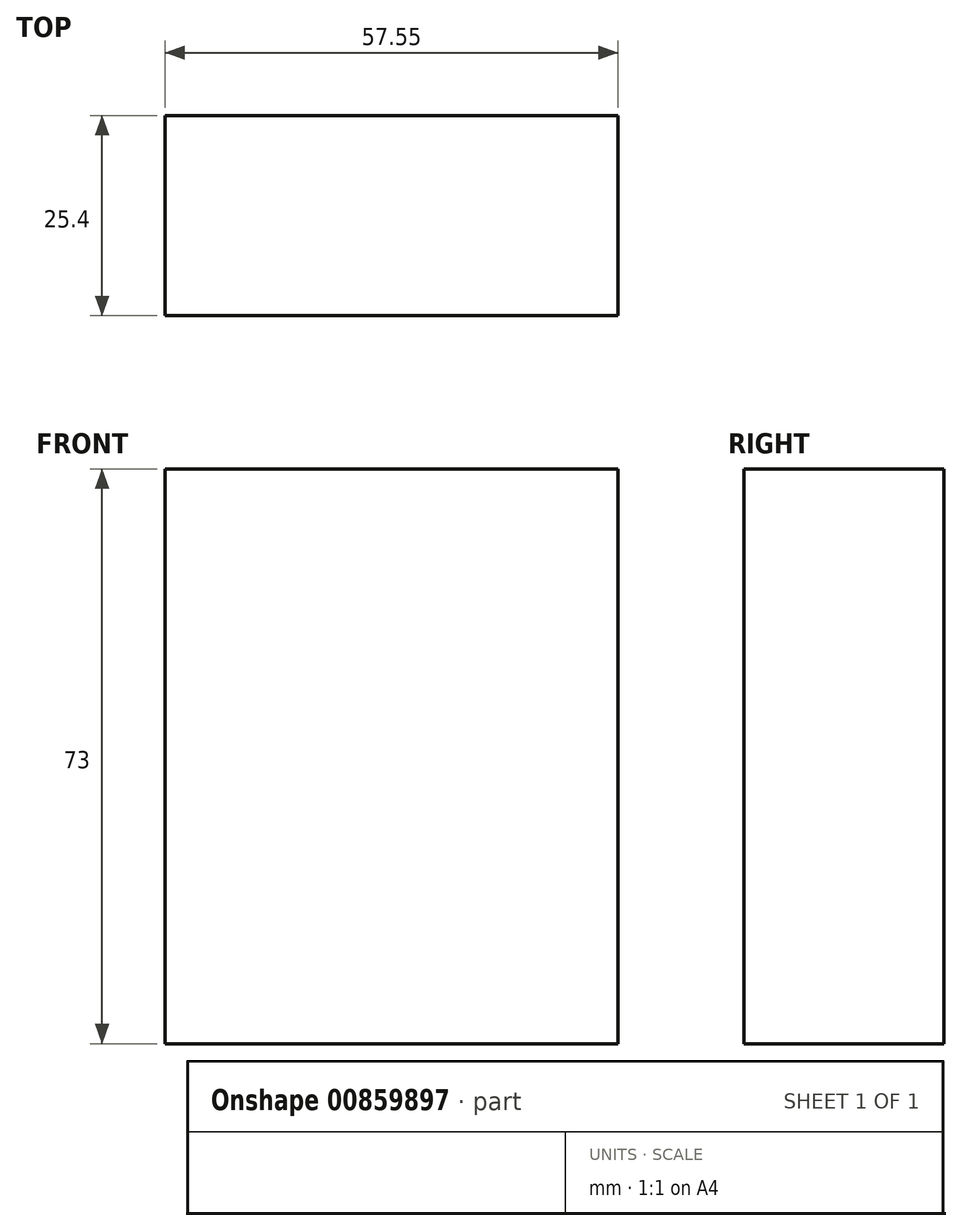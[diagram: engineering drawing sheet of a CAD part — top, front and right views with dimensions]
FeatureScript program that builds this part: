
annotation { "Feature Type Name" : "Feature", "Feature Type Description" : "" }
export const myFeature = defineFeature(function(context is Context, id is Id, definition is map)
    precondition{}
    {
        {
            var Q0;
            Q0=qCreatedBy(makeId("Front.planeOp"),FACE);
            var sketch = newSketch(context, id + "F0", { "sketchPlane" : qUnion([Q0])});
            skLineSegment(sketch, "E0.bottom", {"start": v(-26.81, 32.7) * mm, "end": v(30.74, 32.7) * mm});
            skLineSegment(sketch, "E0.top", {"start": v(-26.81, -40.29) * mm, "end": v(30.74, -40.29) * mm});
            skLineSegment(sketch, "E0.left", {"start": v(-26.81, 32.7) * mm, "end": v(-26.81, -40.29) * mm});
            skLineSegment(sketch, "E0.right", {"start": v(30.74, 32.7) * mm, "end": v(30.74, -40.29) * mm});
            skSolve(sketch);
        }
        {
            var Q0;
            Q0 = qSketchRegion(id + "F0", true);
            extrude(context, id + "F1", {"entities" : qUnion([Q0]), "depth" : 25.4 * mm, "offsetDistance" : 25.4 * mm});
        }
    });
